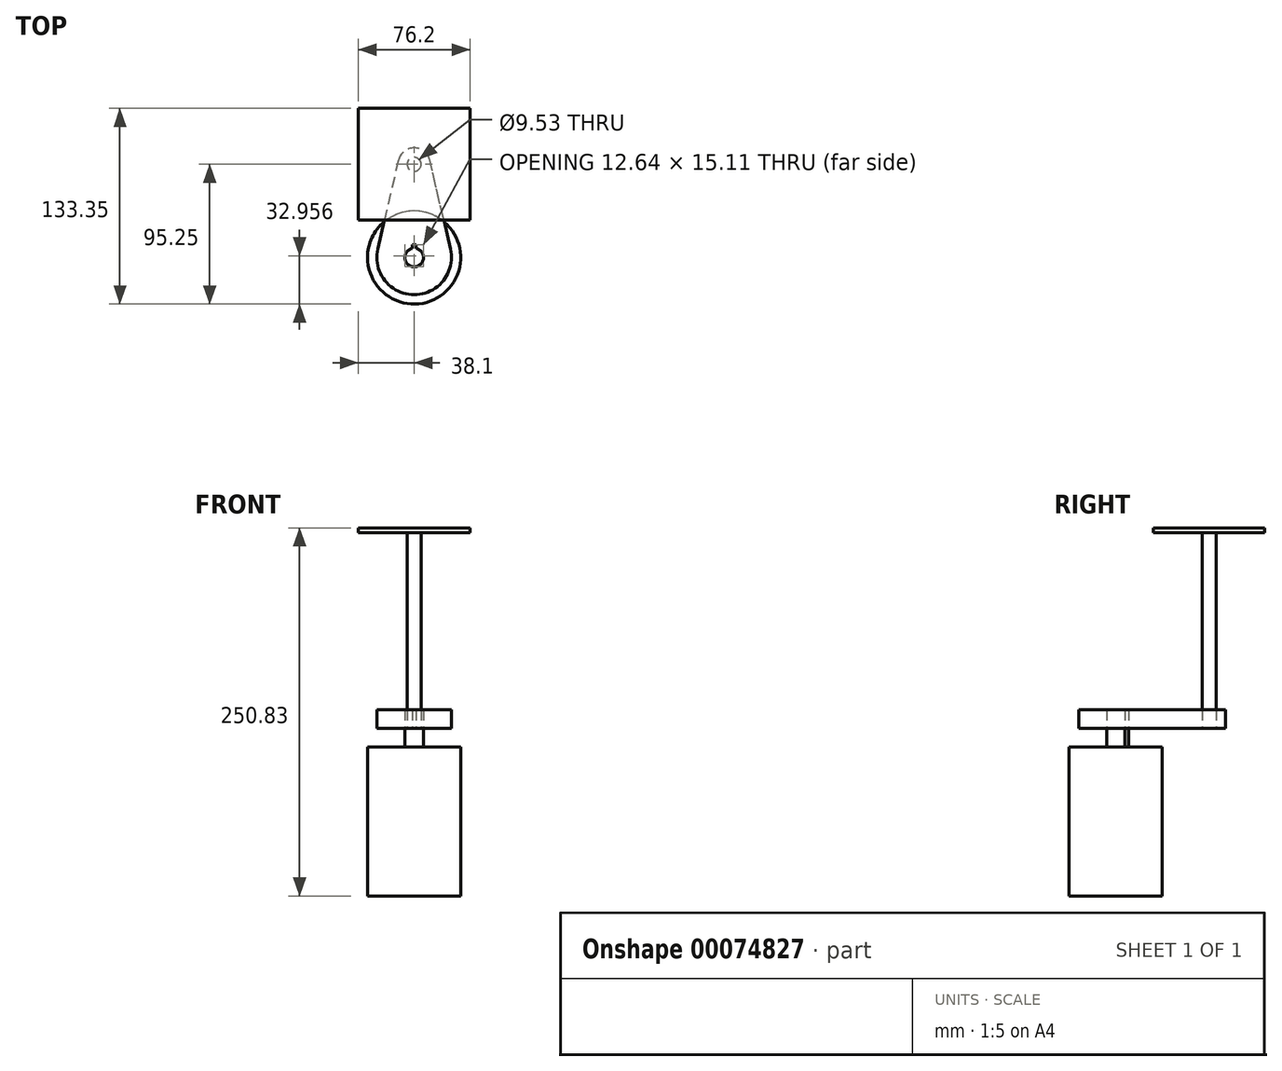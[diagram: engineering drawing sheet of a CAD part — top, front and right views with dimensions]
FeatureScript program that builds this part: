
annotation { "Feature Type Name" : "Feature", "Feature Type Description" : "" }
export const myFeature = defineFeature(function(context is Context, id is Id, definition is map)
    precondition{}
    {
        {
            var Q0;
            Q0=qCreatedBy(makeId("Top.planeOp"),FACE);
            var sketch = newSketch(context, id + "F0", { "sketchPlane" : qUnion([Q0])});
            skArc(sketch, "E0", {"start": v(-1.27, 6.22) * mm, "mid": v(0, -6.35) * mm, "end": v(1.27, 6.22) * mm});
            skLineSegment(sketch, "E1.top", {"start": v(-1.27, 8.76) * mm, "end": v(1.27, 8.76) * mm});
            skLineSegment(sketch, "E1.left", {"start": v(-1.27, 6.22) * mm, "end": v(-1.27, 8.76) * mm});
            skLineSegment(sketch, "E1.right", {"start": v(1.27, 6.22) * mm, "end": v(1.27, 8.76) * mm});
            skPoint(sketch, "E1.middle", {"position": v(0, 7.5) * mm});
            skSolve(sketch);
        }
        {
            var Q0;
            Q0 = qSketchRegion(id + "F0", true);
            extrude(context, id + "F1", {"entities" : qUnion([Q0]), "oppositeDirection" : true, "depth" : 19.05 * mm, "hasSecondDirection" : true, "secondDirectionOppositeDirection" : false, "secondDirectionDepth" : 6.35 * mm});
        }
        {
            var Q0;
            Q0=makeQuery(id+"F1.opExtrude","CAP_FACE",FACE,{"disambiguationData":[OSD([sQuery(id+"F0.wireOp",EDGE,"E0"),sQuery(id+"F0.wireOp",EDGE,"E1.top"),sQuery(id+"F0.wireOp",EDGE,"E1.left"),sQuery(id+"F0.wireOp",EDGE,"E1.right")])],"isStart":false});
            var sketch = newSketch(context, id + "F2", { "sketchPlane" : qUnion([Q0])});
            skCircle(sketch, "E2", {"center": v(0, 0) * mm, "radius": 31.75 * mm});
            skSolve(sketch);
        }
        {
            var Q0;
            Q0 = qSketchRegion(id + "F2", true);
            extrude(context, id + "F3", {"entities" : qUnion([Q0]), "operationType" : NewBodyOperationType.ADD, "depth" : 101.6 * mm});
        }
        {
            var Q0;
            Q0=qCreatedBy(makeId("Top.planeOp"),FACE);
            var sketch = newSketch(context, id + "F4", { "sketchPlane" : qUnion([Q0])});
            skCircle(sketch, "E3", {"center": v(0, 63.5) * mm, "radius": 4.76 * mm});
            skSolve(sketch);
        }
        {
            var Q0;
            Q0 = qSketchRegion(id + "F4", true);
            extrude(context, id + "F5", {"entities" : qUnion([Q0]), "depth" : 127 * mm, "hasSecondDirection" : true, "secondDirectionOppositeDirection" : true, "secondDirectionDepth" : 6.35 * mm});
        }
        {
            var Q0;
            Q0=qCreatedBy(makeId("Top.planeOp"),FACE);
            var sketch = newSketch(context, id + "F6", { "sketchPlane" : qUnion([Q0])});
            skArc(sketch, "E4.0", {"start": v(-1.27, 6.22) * mm, "mid": v(0, -6.35) * mm, "end": v(1.27, 6.22) * mm});
            skLineSegment(sketch, "E4.1", {"start": v(-1.27, 6.22) * mm, "end": v(-1.27, 8.76) * mm});
            skLineSegment(sketch, "E4.2", {"start": v(-1.27, 8.76) * mm, "end": v(1.27, 8.76) * mm});
            skLineSegment(sketch, "E4.3", {"start": v(1.27, 6.22) * mm, "end": v(1.27, 8.76) * mm});
            skCircle(sketch, "E5.0", {"center": v(0, 63.5) * mm, "radius": 4.76 * mm});
            skCircle(sketch, "E6", {"center": v(0, 63.5) * mm, "radius": 11.11 * mm, "construction": true});
            skCircle(sketch, "E7", {"center": v(0, 0) * mm, "radius": 25.4 * mm, "construction": true});
            skLineSegment(sketch, "E8", {"start": v(-10.83, 66) * mm, "end": v(-24.75, 5.72) * mm});
            skLineSegment(sketch, "E9", {"start": v(24.75, 5.72) * mm, "end": v(10.83, 66) * mm});
            skArc(sketch, "E10", {"start": v(-10.83, 66) * mm, "mid": v(0, 74.61) * mm, "end": v(10.83, 66) * mm});
            skArc(sketch, "E11", {"start": v(24.75, 5.71) * mm, "mid": v(0, -25.4) * mm, "end": v(-24.75, 5.71) * mm});
            skSolve(sketch);
        }
        {
            var Q0;
            Q0 = qSketchRegion(id + "F6", true);
            extrude(context, id + "F7", {"entities" : qUnion([Q0]), "depth" : 6.35 * mm, "hasSecondDirection" : true, "secondDirectionOppositeDirection" : true, "secondDirectionDepth" : 6.35 * mm});
        }
        {
            var Q0;
            Q0=makeQuery(id+"F5.opExtrude","CAP_FACE",FACE,{"disambiguationData":[OSD([sQuery(id+"F4.wireOp",EDGE,"E3")])],"isStart":false});
            var sketch = newSketch(context, id + "F8", { "sketchPlane" : qUnion([Q0])});
            skLineSegment(sketch, "E12.bottom", {"start": v(-38.1, 101.6) * mm, "end": v(38.1, 101.6) * mm});
            skLineSegment(sketch, "E12.top", {"start": v(-38.1, 25.4) * mm, "end": v(38.1, 25.4) * mm});
            skLineSegment(sketch, "E12.left", {"start": v(-38.1, 101.6) * mm, "end": v(-38.1, 25.4) * mm});
            skLineSegment(sketch, "E12.right", {"start": v(38.1, 101.6) * mm, "end": v(38.1, 25.4) * mm});
            skPoint(sketch, "E12.middle", {"position": v(0, 63.5) * mm});
            skSolve(sketch);
        }
        {
            var Q0;
            Q0 = qSketchRegion(id + "F8", true);
            extrude(context, id + "F9", {"entities" : qUnion([Q0]), "depth" : 3.17 * mm});
        }
    });
